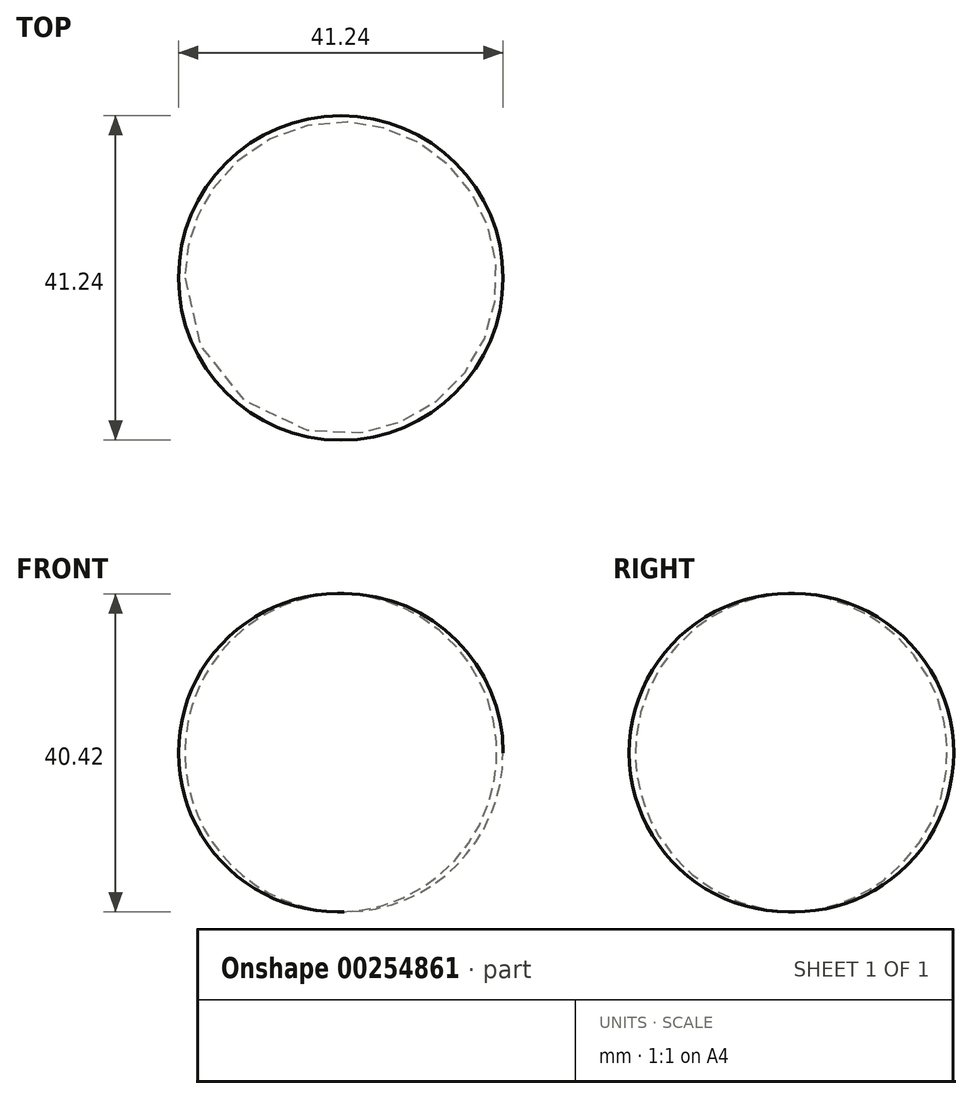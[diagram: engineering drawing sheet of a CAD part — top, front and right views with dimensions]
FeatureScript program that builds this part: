
annotation { "Feature Type Name" : "Feature", "Feature Type Description" : "" }
export const myFeature = defineFeature(function(context is Context, id is Id, definition is map)
    precondition{}
    {
        {
            var Q0;
            Q0=qCreatedBy(makeId("Front.planeOp"),FACE);
            var sketch = newSketch(context, id + "F0", { "sketchPlane" : qUnion([Q0])});
            skLineSegment(sketch, "E0", {"start": v(0, 40.42) * mm, "end": v(0, 0) * mm});
            skArc(sketch, "E1", {"start": v(0, 0) * mm, "mid": v(19.81, 20.2) * mm, "end": v(0, 40.42) * mm});
            skSolve(sketch);
        }
        {
            var Q0;
            Q0=makeQuery(id+"F0.imprint","IMPRINT",FACE,{"disambiguationData":[TD([[makeQuery(id+"F0.imprint","IMPRINT",EDGE,{"derivedFrom":sQuery(id+"F0.wireOp",EDGE,"E0")}),1.0]])]});
            var Q1;
            Q1=sQuery(id+"F0.wireOp",EDGE,"E0");
            revolve(context, id + "F1", {"entities" : qUnion([Q0]), "axis" : qUnion([Q1]), "revolveType" : RevolveType.FULL});
        }
    });
